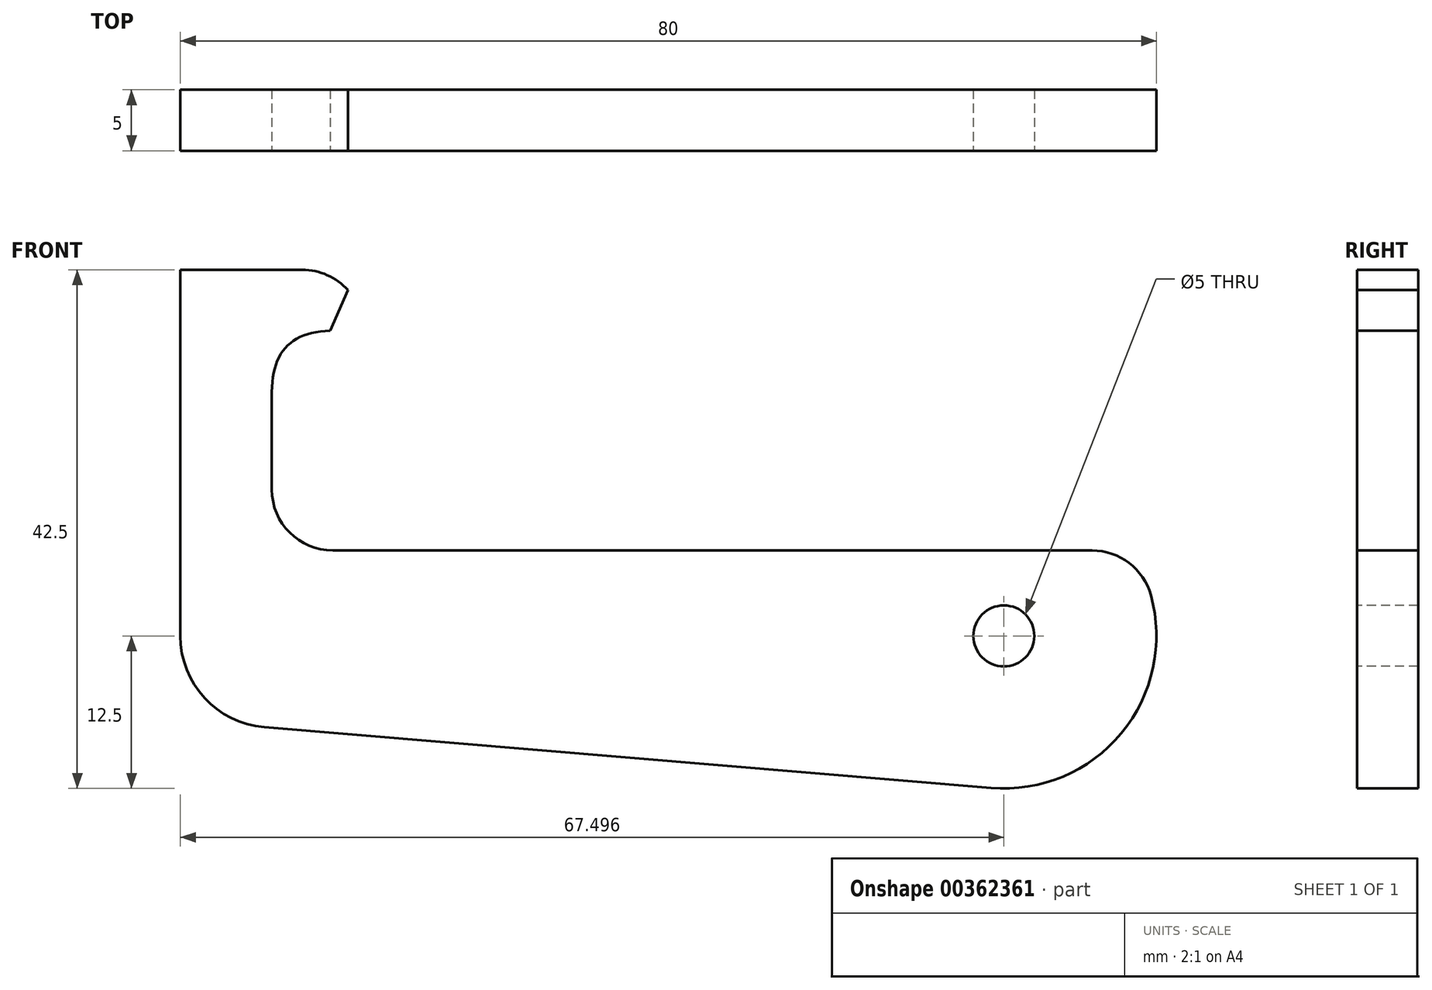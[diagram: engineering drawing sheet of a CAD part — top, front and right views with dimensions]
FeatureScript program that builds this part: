
annotation { "Feature Type Name" : "Feature", "Feature Type Description" : "" }
export const myFeature = defineFeature(function(context is Context, id is Id, definition is map)
    precondition{}
    {
        {
            var Q0;
            Q0=qCreatedBy(makeId("Front.planeOp"),FACE);
            var sketch = newSketch(context, id + "F0", { "sketchPlane" : qUnion([Q0])});
            skCircle(sketch, "E0", {"center": v(14.4, 0) * mm, "radius": 12.5 * mm});
            skCircle(sketch, "E1", {"center": v(-45.6, 0) * mm, "radius": 7.5 * mm});
            skLineSegment(sketch, "E2", {"start": v(-46.23, 7.47) * mm, "end": v(13.35, 12.46) * mm});
            skLineSegment(sketch, "E3", {"start": v(-46.23, -7.47) * mm, "end": v(13.35, -12.46) * mm});
            skLineSegment(sketch, "E4.bottom", {"start": v(-45.6, 0) * mm, "end": v(-53.1, 0) * mm});
            skLineSegment(sketch, "E5.bottom", {"start": v(-53.1, 0) * mm, "end": v(-45.6, 0) * mm});
            skLineSegment(sketch, "E5.top", {"start": v(-53.1, 30) * mm, "end": v(-45.6, 30) * mm});
            skLineSegment(sketch, "E5.left", {"start": v(-53.1, 0) * mm, "end": v(-53.1, 30) * mm});
            skLineSegment(sketch, "E5.right", {"start": v(-45.6, 0) * mm, "end": v(-45.6, 30) * mm});
            skLineSegment(sketch, "E6.bottom", {"start": v(-53.1, 30) * mm, "end": v(-38.1, 30) * mm});
            skLineSegment(sketch, "E6.top", {"start": v(-53.1, 25) * mm, "end": v(-38.1, 25) * mm});
            skLineSegment(sketch, "E6.left", {"start": v(-53.1, 30) * mm, "end": v(-53.1, 25) * mm});
            skLineSegment(sketch, "E6.right", {"start": v(-38.1, 30) * mm, "end": v(-38.1, 25) * mm});
            skSolve(sketch);
        }
        {
            var Q0;
            Q0 = qSketchRegion(id + "F0", true);
            extrude(context, id + "F1", {"entities" : qUnion([Q0]), "depth" : 2.5 * mm, "hasSecondDirection" : true, "secondDirectionOppositeDirection" : true, "secondDirectionDepth" : 2.5 * mm});
        }
        {
            var Q0;
            Q0=makeQuery(id+"F1.opExtrude","CAP_FACE",FACE,{"disambiguationData":[OSD([sQuery(id+"F0.wireOp",EDGE,"E0"),sQuery(id+"F0.wireOp",EDGE,"E1"),sQuery(id+"F0.wireOp",EDGE,"E2"),sQuery(id+"F0.wireOp",EDGE,"E3")])],"isStart":false});
            var sketch = newSketch(context, id + "F2", { "sketchPlane" : qUnion([Q0])});
            skLineSegment(sketch, "E7", {"start": v(26.9, 0) * mm, "end": v(14.4, 0) * mm});
            skLineSegment(sketch, "E8", {"start": v(14.4, 0) * mm, "end": v(0, 0) * mm});
            skLineSegment(sketch, "E9.bottom", {"start": v(-45.6, 7) * mm, "end": v(45.6, 7) * mm});
            skLineSegment(sketch, "E9.top", {"start": v(-45.6, 17) * mm, "end": v(45.6, 17) * mm});
            skLineSegment(sketch, "E9.left", {"start": v(-45.6, 7) * mm, "end": v(-45.6, 17) * mm});
            skLineSegment(sketch, "E9.right", {"start": v(45.6, 7) * mm, "end": v(45.6, 17) * mm});
            skPoint(sketch, "E9.middle", {"position": v(0, 12) * mm});
            skSolve(sketch);
        }
        {
            var Q0;
            Q0=sQuery(id+"F2.wireOp",VERTEX,"E8.start");
            var Q1;
            Q1=makeQuery(id+"F1.opExtrude","SWEPT_BODY",BODY,{"disambiguationData":[OSD([sQuery(id+"F0.wireOp",EDGE,"E0"),sQuery(id+"F0.wireOp",EDGE,"E1"),sQuery(id+"F0.wireOp",EDGE,"E2"),sQuery(id+"F0.wireOp",EDGE,"E3")])]});
            hole(context, id + "F3", {"style" : HoleStyle.SIMPLE, "endStyle" : HoleEndStyle.THROUGH, "holeDiameter" : 5 * mm, "isTappedThrough" : true, "tappedDepth" : 12 * mm, "tapClearance" : 3, "locations" : qUnion([Q0]), "scope" : qUnion([Q1])});
        }
        {
            var Q0;
            Q0 = qSketchRegion(id + "F2", true);
            extrude(context, id + "F4", {"entities" : qUnion([Q0]), "operationType" : NewBodyOperationType.REMOVE, "oppositeDirection" : true, "depth" : 25 * mm});
        }
        {
            var Q0;
            Q0=makeQuery(id+"F4.boolean.opBoolean","INTERSECT",EDGE,{"derivedFrom":[makeQuery(id+"F1.opExtrude","SWEPT_FACE",FACE,{"disambiguationData":[OSD([sQuery(id+"F0.wireOp",EDGE,"E0")])]}),makeQuery(id+"F4.opExtrude","SWEPT_FACE",FACE,{"disambiguationData":[OSD([sQuery(id+"F2.wireOp",EDGE,"E9.bottom")])]})]});
            fillet(context, id + "F5", {"entities" : qUnion([Q0]), "radius" : 5 * mm, "tangentPropagation" : true, "allowEdgeOverflow" : false});
        }
        {
            var Q0;
            Q0=makeQuery(id+"F4.boolean.opBoolean","COPY",EDGE,{"derivedFrom":makeQuery(id+"F4.opExtrude","SWEPT_EDGE",EDGE,{"disambiguationData":[OSD([sQuery(id+"F2.wireOp",EDGE,"E9.bottom"),sQuery(id+"F2.wireOp",EDGE,"E9.left")])]})});
            fillet(context, id + "F6", {"entities" : qUnion([Q0]), "radius" : 5 * mm, "tangentPropagation" : true, "allowEdgeOverflow" : false});
        }
        {
            var Q0;
            Q0=makeQuery(id+"F1.opExtrude","SWEPT_EDGE",EDGE,{"disambiguationData":[OSD([sQuery(id+"F0.wireOp",EDGE,"E5.right"),sQuery(id+"F0.wireOp",EDGE,"E6.top")])]});
            fillet(context, id + "F7", {"entities" : qUnion([Q0]), "radius" : 5 * mm, "tangentPropagation" : true, "rho" : 0.5, "crossSection" : FilletCrossSection.CONIC, "allowEdgeOverflow" : false});
        }
        {
            var Q0;
            Q0=makeQuery(id+"F1.opExtrude","SWEPT_EDGE",EDGE,{"disambiguationData":[OSD([sQuery(id+"F0.wireOp",EDGE,"E6.bottom"),sQuery(id+"F0.wireOp",EDGE,"E6.right")])]});
            var Q1;
            Q1=makeQuery(id+"F1.opExtrude","SWEPT_EDGE",EDGE,{"disambiguationData":[OSD([sQuery(id+"F0.wireOp",EDGE,"E6.bottom"),sQuery(id+"F0.wireOp",EDGE,"E6.left")])]});
            fillet(context, id + "F8", {"entities" : qUnion([Q0, Q1]), "radius" : 5 * mm, "tangentPropagation" : true, "allowEdgeOverflow" : false});
        }
        {
            var Q0;
            Q0=makeQuery(id+"F8.opFillet","BLEND_EDGE",EDGE,{"blendedFrom":[makeQuery(id+"F1.opExtrude","SWEPT_EDGE",EDGE,{"disambiguationData":[OSD([sQuery(id+"F0.wireOp",EDGE,"E6.bottom"),sQuery(id+"F0.wireOp",EDGE,"E6.right")])]}),makeQuery(id+"F1.opExtrude","SWEPT_FACE",FACE,{"disambiguationData":[OSD([sQuery(id+"F0.wireOp",EDGE,"E6.top")])]})],"blendedInto":[makeQuery(id+"F1.opExtrude","SWEPT_FACE",FACE,{"disambiguationData":[OSD([sQuery(id+"F0.wireOp",EDGE,"E6.top")])]})]});
            chamfer(context, id + "F9", {"entities" : qUnion([Q0]), "width" : 2 * mm, "tangentPropagation" : true});
        }
    });
